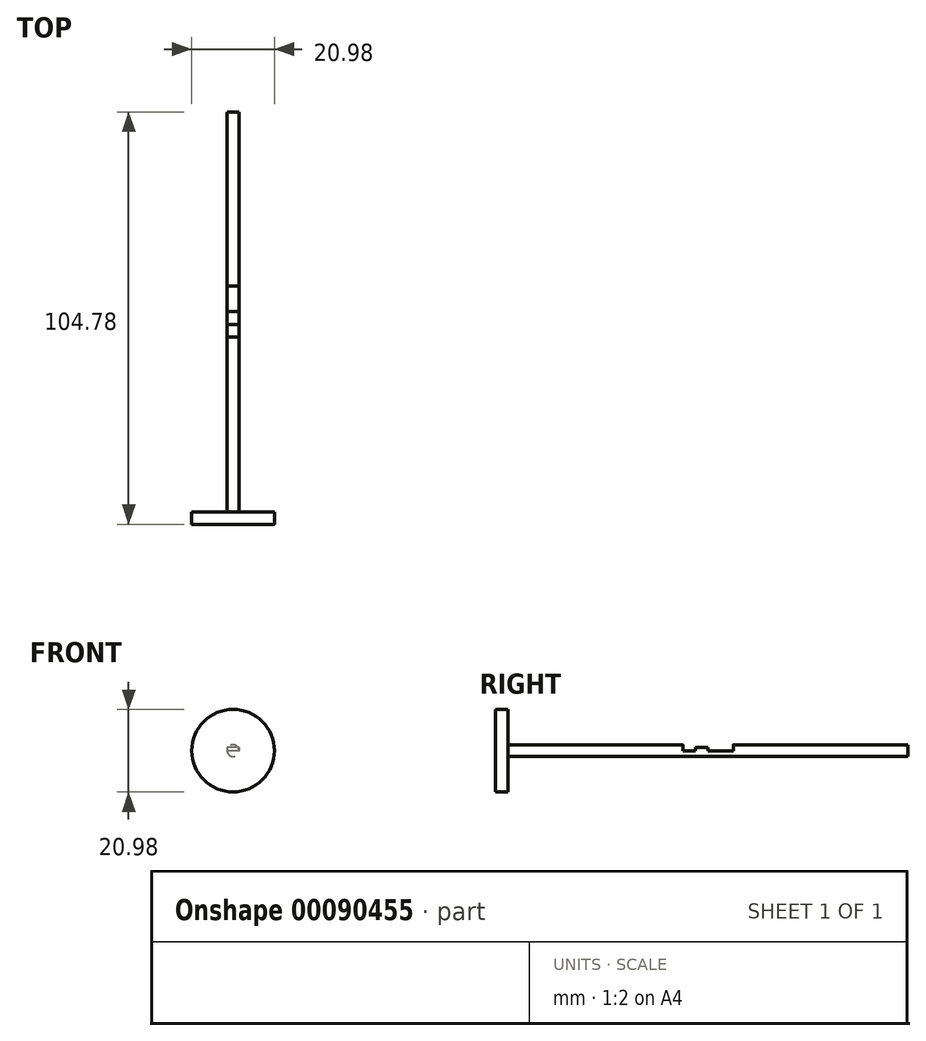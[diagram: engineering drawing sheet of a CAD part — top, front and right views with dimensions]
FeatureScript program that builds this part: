
annotation { "Feature Type Name" : "Feature", "Feature Type Description" : "" }
export const myFeature = defineFeature(function(context is Context, id is Id, definition is map)
    precondition{}
    {
        {
            var Q0;
            Q0=qCreatedBy(makeId("Front.planeOp"),FACE);
            var sketch = newSketch(context, id + "F0", { "sketchPlane" : qUnion([Q0])});
            skCircle(sketch, "E0", {"center": v(0, 0) * mm, "radius": 1.5 * mm});
            skSolve(sketch);
        }
        {
            var Q0;
            Q0=qSketchRegion(id+"F0",true);
            extrude(context, id + "F1", {"entities" : qUnion([Q0]), "depth" : 101.6 * mm});
        }
        {
            var Q0;
            Q0=makeQuery(id+"F1.opExtrude","CAP_FACE",FACE,{"disambiguationData":[OSD([sQuery(id+"F0.wireOp",EDGE,"E0")])],"isStart":false});
            var sketch = newSketch(context, id + "F2", { "sketchPlane" : qUnion([Q0])});
            skCircle(sketch, "E1", {"center": v(0, 0) * mm, "radius": 10.49 * mm});
            skSolve(sketch);
        }
        {
            var Q0;
            Q0=qSketchRegion(id+"F2",true);
            extrude(context, id + "F3", {"entities" : qUnion([Q0]), "operationType" : NewBodyOperationType.ADD, "depth" : 3.17 * mm});
        }
        {
            var Q0;
            Q0=qCreatedBy(makeId("Top.planeOp"),FACE);
            var sketch = newSketch(context, id + "F4", { "sketchPlane" : qUnion([Q0])});
            skLineSegment(sketch, "E2.bottom", {"start": v(-5.08, -44.26) * mm, "end": v(5.08, -44.26) * mm});
            skLineSegment(sketch, "E2.top", {"start": v(-5.08, -57.14) * mm, "end": v(5.08, -57.14) * mm});
            skLineSegment(sketch, "E2.left", {"start": v(-5.08, -44.26) * mm, "end": v(-5.08, -57.14) * mm});
            skLineSegment(sketch, "E2.right", {"start": v(5.08, -44.26) * mm, "end": v(5.08, -57.14) * mm});
            skSolve(sketch);
        }
        {
            var Q0;
            Q0=makeQuery(id+"F4.imprint","IMPRINT",FACE,{"disambiguationData":[TD([[makeQuery(id+"F4.imprint","IMPRINT",EDGE,{"derivedFrom":sQuery(id+"F4.wireOp",EDGE,"E2.bottom")}),-1.0]])]});
            extrude(context, id + "F5", {"entities" : qUnion([Q0]), "operationType" : NewBodyOperationType.REMOVE, "depth" : 20.24 * mm});
        }
        {
            var Q0;
            Q0=makeQuery(id+"F5.boolean.opBoolean","COPY",FACE,{"derivedFrom":makeQuery(id+"F5.opExtrude","SWEPT_FACE",FACE,{"disambiguationData":[OSD([sQuery(id+"F4.wireOp",EDGE,"E2.bottom")])]})});
            var sketch = newSketch(context, id + "F6", { "sketchPlane" : qUnion([Q0])});
            skLineSegment(sketch, "E3.bottom", {"start": v(-0.6, 1.38) * mm, "end": v(1.32, 1.38) * mm});
            skLineSegment(sketch, "E3.top", {"start": v(-0.6, 0.14) * mm, "end": v(1.32, 0.14) * mm});
            skLineSegment(sketch, "E3.left", {"start": v(-0.6, 1.38) * mm, "end": v(-0.6, 0.14) * mm});
            skLineSegment(sketch, "E3.right", {"start": v(1.32, 1.38) * mm, "end": v(1.32, 0.14) * mm});
            skSolve(sketch);
        }
        {
            var Q0;
            Q0=makeQuery(id+"F6.imprint","IMPRINT",FACE,{"disambiguationData":[TD([[makeQuery(id+"F6.imprint","IMPRINT",EDGE,{"derivedFrom":sQuery(id+"F6.wireOp",EDGE,"E3.bottom")}),-1.0]])]});
            extrude(context, id + "F7", {"entities" : qUnion([Q0]), "operationType" : NewBodyOperationType.ADD, "depth" : 8.97 * mm});
        }
        {
            var Q0;
            Q0=makeQuery(id+"F7.opExtrude","SWEPT_BODY",BODY,{"disambiguationData":[OSD([sQuery(id+"F0.wireOp",EDGE,"E0"),sQuery(id+"F4.wireOp",EDGE,"E2.bottom"),sQuery(id+"F6.wireOp",EDGE,"E3.bottom"),sQuery(id+"F6.wireOp",EDGE,"E3.right")])]});
            deleteBodies(context, id + "F8", {"entities" : qUnion([Q0])});
        }
        {
            var Q0;
            Q0=makeQuery(id+"F5.boolean.opBoolean","COPY",FACE,{"derivedFrom":makeQuery(id+"F5.opExtrude","CAP_FACE",FACE,{"disambiguationData":[OSD([sQuery(id+"F4.wireOp",EDGE,"E2.bottom"),sQuery(id+"F4.wireOp",EDGE,"E2.top"),sQuery(id+"F4.wireOp",EDGE,"E2.left"),sQuery(id+"F4.wireOp",EDGE,"E2.right")])],"isStart":true})});
            var sketch = newSketch(context, id + "F9", { "sketchPlane" : qUnion([Q0])});
            skLineSegment(sketch, "E4.bottom", {"start": v(1.5, -50.7) * mm, "end": v(-1.5, -50.7) * mm});
            skLineSegment(sketch, "E4.top", {"start": v(1.5, -53.95) * mm, "end": v(-1.5, -53.95) * mm});
            skLineSegment(sketch, "E4.left", {"start": v(1.5, -50.7) * mm, "end": v(1.5, -53.95) * mm});
            skLineSegment(sketch, "E4.right", {"start": v(-1.5, -50.7) * mm, "end": v(-1.5, -53.95) * mm});
            skSolve(sketch);
        }
        {
            var Q0;
            Q0=makeQuery(id+"F9.imprint","IMPRINT",FACE,{"disambiguationData":[TD([[makeQuery(id+"F9.imprint","IMPRINT",EDGE,{"derivedFrom":sQuery(id+"F9.wireOp",EDGE,"E4.bottom")}),1.0]])]});
            extrude(context, id + "F10", {"entities" : qUnion([Q0]), "operationType" : NewBodyOperationType.ADD, "depth" : 0.77 * mm});
        }
    });
